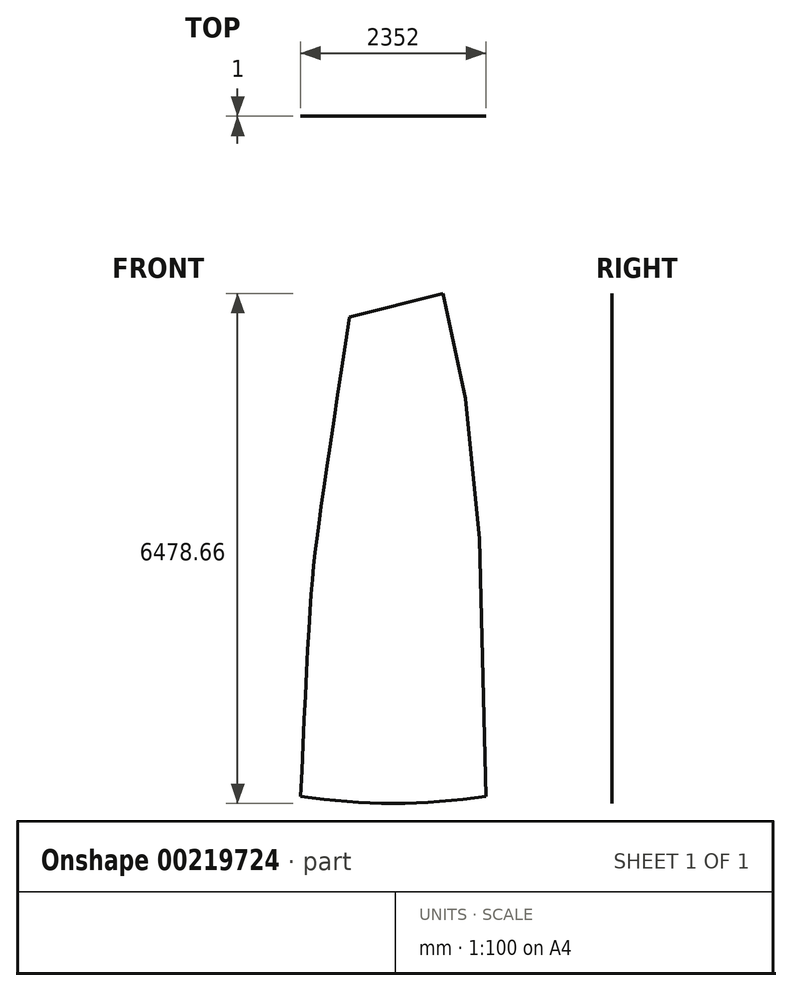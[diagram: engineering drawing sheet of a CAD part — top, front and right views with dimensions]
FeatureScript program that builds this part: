
annotation { "Feature Type Name" : "Feature", "Feature Type Description" : "" }
export const myFeature = defineFeature(function(context is Context, id is Id, definition is map)
    precondition{}
    {
        {
            var Q0;
            Q0=qCreatedBy(makeId("Front.planeOp"),FACE);
            var sketch = newSketch(context, id + "F0", { "sketchPlane" : qUnion([Q0])});
            skLineSegment(sketch, "E0", {"start": v(0, 0) * mm, "end": v(2352, 0) * mm});
            skLineSegment(sketch, "E1", {"start": v(0, 0) * mm, "end": v(620.2, 6088.5) * mm});
            skLineSegment(sketch, "E2", {"start": v(620.2, 6088.5) * mm, "end": v(2352, 0) * mm});
            skLineSegment(sketch, "E3", {"start": v(620.2, 6088.5) * mm, "end": v(1841.93, 6177.86) * mm});
            skLineSegment(sketch, "E4", {"start": v(1841.93, 6177.86) * mm, "end": v(2352, 0) * mm});
            skSolve(sketch);
        }
        {
            var Q0;
            Q0=makeQuery(id+"F0.imprint","IMPRINT",FACE,{"disambiguationData":[TD([[makeQuery(id+"F0.imprint","IMPRINT",EDGE,{"derivedFrom":sQuery(id+"F0.wireOp",EDGE,"E0")}),1.0]])]});
            var sketch = newSketch(context, id + "F1", { "sketchPlane" : qUnion([Q0])});
            skLineSegment(sketch, "E5", {"start": v(620.2, 6088.5) * mm, "end": v(1807.85, 6388.66) * mm});
            skLineSegment(sketch, "E6", {"start": v(1807.85, 6388.66) * mm, "end": v(2352, 0) * mm});
            skLineSegment(sketch, "E7", {"start": v(620.2, 6088.5) * mm, "end": v(2352, 0) * mm});
            skSolve(sketch);
        }
        {
            var Q0;
            Q0=makeQuery(id+"F0.imprint","IMPRINT",FACE,{"disambiguationData":[TD([[makeQuery(id+"F0.imprint","IMPRINT",EDGE,{"derivedFrom":sQuery(id+"F0.wireOp",EDGE,"E0")}),1.0]])]});
            var sketch = newSketch(context, id + "F2", { "sketchPlane" : qUnion([Q0])});
            skArc(sketch, "E8", {"start": v(0, 0) * mm, "mid": v(1176, -90) * mm, "end": v(2352, 0) * mm});
            skLineSegment(sketch, "E9", {"start": v(620.2, 6088.5) * mm, "end": v(1807.85, 6388.66) * mm});
            skFitSpline(sketch, "E10", {"points": [v(0, 0) * mm, v(127.67, 2496.74) * mm, v(233.1, 3492.23) * mm, v(620.2, 6088.5) * mm], "startDerivative": vector(340.46, 7570.42) * mm, "endDerivative": vector(1177.6, 7705.28) * mm});
            skPoint(sketch, "E11", {"position": v(1486.1, 3044.25) * mm});
            skLineSegment(sketch, "E12", {"start": v(1486.1, 3044.25) * mm, "end": v(3056.8, 3491.02) * mm, "construction": true});
            skLineSegment(sketch, "E13", {"start": v(2271.45, 3267.63) * mm, "end": v(243.3, 3566.19) * mm, "construction": true});
            skLineSegment(sketch, "E14", {"start": v(620.2, 6088.5) * mm, "end": v(2271.45, 3267.63) * mm, "construction": true});
            skPoint(sketch, "E15", {"position": v(1445.82, 4678.06) * mm});
            skLineSegment(sketch, "E16", {"start": v(2091.02, 5055.74) * mm, "end": v(495.54, 5271.52) * mm, "construction": true});
            skLineSegment(sketch, "E17", {"start": v(1445.82, 4678.06) * mm, "end": v(2308.84, 5183.25) * mm, "construction": true});
            skLineSegment(sketch, "E18", {"start": v(2091.02, 5055.74) * mm, "end": v(620.2, 6088.5) * mm, "construction": true});
            skPoint(sketch, "E19", {"position": v(1355.6, 5572.12) * mm});
            skLineSegment(sketch, "E20", {"start": v(1355.6, 5572.12) * mm, "end": v(1930.26, 6390.52) * mm, "construction": true});
            skLineSegment(sketch, "E21", {"start": v(1652.3, 5994.67) * mm, "end": v(607.35, 6004.43) * mm, "construction": true});
            skLineSegment(sketch, "E22", {"start": v(2352, 0) * mm, "end": v(2271.45, 3267.63) * mm});
            skLineSegment(sketch, "E23", {"start": v(2091.02, 5055.74) * mm, "end": v(2271.45, 3267.63) * mm});
            skLineSegment(sketch, "E24", {"start": v(2091.02, 5055.74) * mm, "end": v(1807.85, 6388.66) * mm});
            skSolve(sketch);
        }
        {
            var Q0;
            Q0=qSketchRegion(id+"F2",true);
            extrude(context, id + "F3", {"entities" : qUnion([Q0]), "depth" : 1 * mm});
        }
    });
